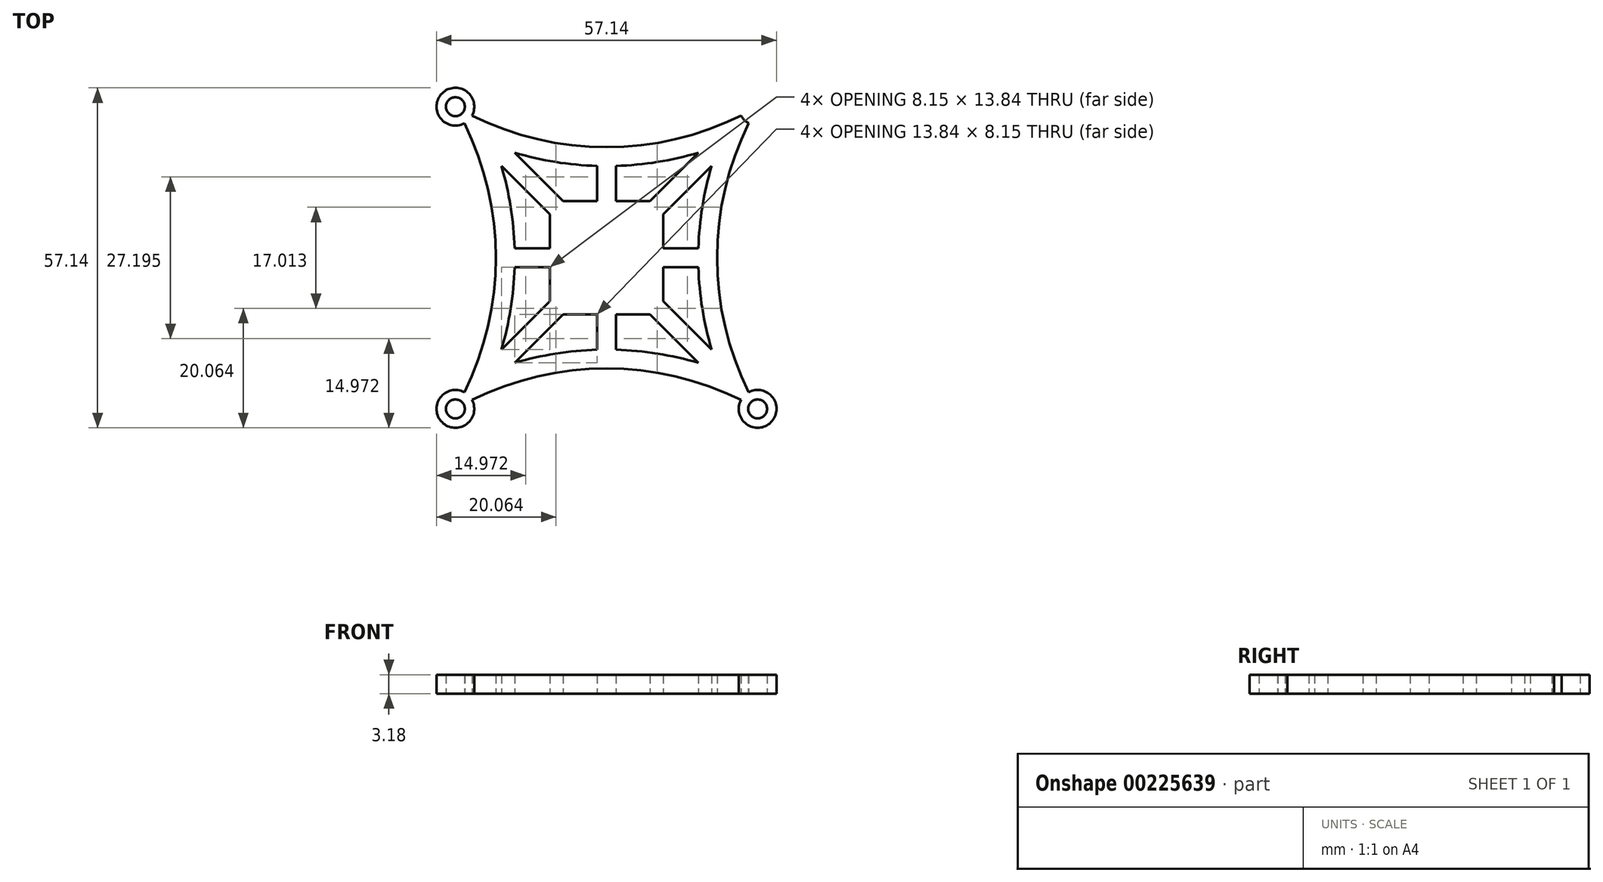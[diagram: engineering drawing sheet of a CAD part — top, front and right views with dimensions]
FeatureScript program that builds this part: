
annotation { "Feature Type Name" : "Feature", "Feature Type Description" : "" }
export const myFeature = defineFeature(function(context is Context, id is Id, definition is map)
    precondition{}
    {
        {
            var Q0;
            Q0=qCreatedBy(makeId("Top.planeOp"),FACE);
            var sketch = newSketch(context, id + "F0", { "sketchPlane" : qUnion([Q0])});
            skPoint(sketch, "E0.middle", {"position": v(0, 0) * mm});
            skArc(sketch, "E1", {"start": v(-25.4, -25.4) * mm, "mid": v(-18.6, 0) * mm, "end": v(-25.4, 25.4) * mm});
            skArc(sketch, "E2", {"start": v(25.4, -25.4) * mm, "mid": v(0, -18.6) * mm, "end": v(-25.4, -25.4) * mm});
            skArc(sketch, "E3.MirrorCS", {"start": v(25.4, 25.4) * mm, "mid": v(0, 18.6) * mm, "end": v(-25.4, 25.4) * mm});
            skArc(sketch, "E4.MirrorCS", {"start": v(25.4, -25.4) * mm, "mid": v(18.6, 0) * mm, "end": v(25.4, 25.4) * mm});
            skCircle(sketch, "E5", {"center": v(-25.4, 25.4) * mm, "radius": 3.18 * mm});
            skCircle(sketch, "E6", {"center": v(-25.4, 25.4) * mm, "radius": 1.59 * mm});
            skCircle(sketch, "E7.MirrorC", {"center": v(25.4, 25.4) * mm, "radius": 3.18 * mm});
            skCircle(sketch, "E8.MirrorC", {"center": v(25.4, 25.4) * mm, "radius": 1.59 * mm});
            skCircle(sketch, "E9.MirrorC", {"center": v(25.4, -25.4) * mm, "radius": 3.18 * mm});
            skCircle(sketch, "E10.MirrorC", {"center": v(25.4, -25.4) * mm, "radius": 1.59 * mm});
            skCircle(sketch, "E11.MirrorC", {"center": v(-25.4, -25.4) * mm, "radius": 3.18 * mm});
            skCircle(sketch, "E12.MirrorC", {"center": v(-25.4, -25.4) * mm, "radius": 1.59 * mm});
            skArc(sketch, "E13.0", {"start": v(18.8, 18.8) * mm, "mid": v(0, 15.42) * mm, "end": v(-18.8, 18.8) * mm});
            skArc(sketch, "E13.1", {"start": v(18.8, -18.8) * mm, "mid": v(15.42, 0) * mm, "end": v(18.8, 18.8) * mm});
            skArc(sketch, "E13.2", {"start": v(18.8, -18.8) * mm, "mid": v(0, -15.42) * mm, "end": v(-18.8, -18.8) * mm});
            skArc(sketch, "E13.3", {"start": v(-18.8, -18.8) * mm, "mid": v(-15.42, 0) * mm, "end": v(-18.8, 18.8) * mm});
            skLineSegment(sketch, "E14.top", {"start": v(-1.59, 15.88) * mm, "end": v(1.59, 15.88) * mm});
            skLineSegment(sketch, "E14.left", {"start": v(-1.59, 12.7) * mm, "end": v(-1.59, 15.88) * mm});
            skLineSegment(sketch, "E14.right", {"start": v(1.59, 12.7) * mm, "end": v(1.59, 15.88) * mm});
            skPoint(sketch, "E14.middle", {"position": v(0, 14.29) * mm});
            skLineSegment(sketch, "E15.MirrorCS", {"start": v(1.59, -12.7) * mm, "end": v(1.59, -15.88) * mm});
            skLineSegment(sketch, "E16.MirrorCS", {"start": v(-1.59, -15.88) * mm, "end": v(1.59, -15.88) * mm});
            skLineSegment(sketch, "E17.MirrorCS", {"start": v(-1.59, -12.7) * mm, "end": v(-1.59, -15.88) * mm});
            skLineSegment(sketch, "E18.bottom", {"start": v(-12.7, 1.59) * mm, "end": v(-15.88, 1.59) * mm});
            skLineSegment(sketch, "E18.top", {"start": v(-12.7, -1.59) * mm, "end": v(-15.88, -1.59) * mm});
            skLineSegment(sketch, "E18.right", {"start": v(-15.88, 1.59) * mm, "end": v(-15.88, -1.59) * mm});
            skPoint(sketch, "E18.middle", {"position": v(-14.29, 0) * mm});
            skLineSegment(sketch, "E19.MirrorCS", {"start": v(12.7, 1.59) * mm, "end": v(15.88, 1.59) * mm});
            skLineSegment(sketch, "E20.MirrorCS", {"start": v(12.7, -1.59) * mm, "end": v(15.88, -1.59) * mm});
            skLineSegment(sketch, "E21.MirrorCS", {"start": v(15.88, 1.59) * mm, "end": v(15.88, -1.59) * mm});
            skPoint(sketch, "E22", {"position": v(10.45, 12.7) * mm});
            skPoint(sketch, "E23", {"position": v(12.7, 10.45) * mm});
            skLineSegment(sketch, "E24", {"start": v(10.45, 12.7) * mm, "end": v(15.43, 17.67) * mm});
            skLineSegment(sketch, "E25", {"start": v(12.7, 10.45) * mm, "end": v(17.67, 15.43) * mm});
            skLineSegment(sketch, "E26", {"start": v(17.67, 15.43) * mm, "end": v(15.43, 17.67) * mm});
            skLineSegment(sketch, "E27.MirrorCS", {"start": v(-17.67, 15.43) * mm, "end": v(-15.43, 17.67) * mm});
            skLineSegment(sketch, "E28.MirrorCS", {"start": v(-10.45, 12.7) * mm, "end": v(-15.43, 17.67) * mm});
            skLineSegment(sketch, "E29.MirrorCS", {"start": v(-12.7, 10.45) * mm, "end": v(-17.67, 15.43) * mm});
            skLineSegment(sketch, "E30.MirrorCS", {"start": v(12.7, -10.45) * mm, "end": v(17.67, -15.43) * mm});
            skLineSegment(sketch, "E31.MirrorCS", {"start": v(10.45, -12.7) * mm, "end": v(15.43, -17.67) * mm});
            skLineSegment(sketch, "E32.MirrorCS", {"start": v(17.67, -15.43) * mm, "end": v(15.43, -17.67) * mm});
            skLineSegment(sketch, "E33.MirrorCS", {"start": v(-10.45, -12.7) * mm, "end": v(-15.43, -17.67) * mm});
            skLineSegment(sketch, "E34.MirrorCS", {"start": v(-12.7, -10.45) * mm, "end": v(-17.67, -15.43) * mm});
            skLineSegment(sketch, "E35.bottom", {"start": v(-9.52, 9.53) * mm, "end": v(9.53, 9.53) * mm});
            skLineSegment(sketch, "E35.top", {"start": v(-9.53, -9.53) * mm, "end": v(9.53, -9.53) * mm});
            skLineSegment(sketch, "E35.left", {"start": v(-9.52, 9.53) * mm, "end": v(-9.53, -9.53) * mm});
            skLineSegment(sketch, "E35.right", {"start": v(9.53, 9.53) * mm, "end": v(9.53, -9.53) * mm});
            skLineSegment(sketch, "E36", {"start": v(-10.45, 12.7) * mm, "end": v(-7.28, 9.53) * mm});
            skLineSegment(sketch, "E37", {"start": v(-7.28, 9.53) * mm, "end": v(-9.53, 7.28) * mm});
            skLineSegment(sketch, "E38", {"start": v(-9.52, 7.28) * mm, "end": v(-12.7, 10.45) * mm});
            skLineSegment(sketch, "E39", {"start": v(1.59, 12.7) * mm, "end": v(1.59, 9.53) * mm});
            skLineSegment(sketch, "E40", {"start": v(1.59, 9.53) * mm, "end": v(-1.59, 9.53) * mm});
            skLineSegment(sketch, "E41", {"start": v(-1.59, 9.53) * mm, "end": v(-1.59, 12.7) * mm});
            skLineSegment(sketch, "E42", {"start": v(12.7, 1.59) * mm, "end": v(9.53, 1.59) * mm});
            skLineSegment(sketch, "E43", {"start": v(9.53, 1.59) * mm, "end": v(9.53, -1.59) * mm});
            skLineSegment(sketch, "E44", {"start": v(9.53, -1.59) * mm, "end": v(12.7, -1.59) * mm});
            skLineSegment(sketch, "E45", {"start": v(12.7, -10.45) * mm, "end": v(9.53, -7.28) * mm});
            skLineSegment(sketch, "E46", {"start": v(9.53, -7.28) * mm, "end": v(7.28, -9.53) * mm});
            skLineSegment(sketch, "E47", {"start": v(7.28, -9.53) * mm, "end": v(10.45, -12.7) * mm});
            skLineSegment(sketch, "E48", {"start": v(1.59, -12.7) * mm, "end": v(1.59, -9.53) * mm});
            skLineSegment(sketch, "E49", {"start": v(1.59, -9.53) * mm, "end": v(-1.59, -9.53) * mm});
            skLineSegment(sketch, "E50", {"start": v(-1.59, -9.53) * mm, "end": v(-1.59, -12.7) * mm});
            skLineSegment(sketch, "E51", {"start": v(-17.67, -15.43) * mm, "end": v(-15.43, -17.67) * mm});
            skLineSegment(sketch, "E52", {"start": v(-10.45, -12.7) * mm, "end": v(-7.28, -9.53) * mm});
            skLineSegment(sketch, "E53", {"start": v(-12.7, -10.45) * mm, "end": v(-9.53, -7.28) * mm});
            skLineSegment(sketch, "E54", {"start": v(-9.53, -7.28) * mm, "end": v(-7.28, -9.53) * mm});
            skLineSegment(sketch, "E55", {"start": v(-12.7, 1.59) * mm, "end": v(-9.53, 1.59) * mm});
            skLineSegment(sketch, "E56", {"start": v(-12.7, -1.59) * mm, "end": v(-9.53, -1.59) * mm});
            skLineSegment(sketch, "E57", {"start": v(10.45, 12.7) * mm, "end": v(7.28, 9.53) * mm});
            skLineSegment(sketch, "E58", {"start": v(7.28, 9.53) * mm, "end": v(9.53, 7.28) * mm});
            skLineSegment(sketch, "E59", {"start": v(9.52, 7.28) * mm, "end": v(12.7, 10.45) * mm});
            skSolve(sketch);
        }
        {
            var Q0;
            {var subQ9=sQuery(id+"F0.wireOp",EDGE,"E37");Q0=makeQuery(id+"F0.imprint","IMPRINT",FACE,{"disambiguationData":[TD([[makeQuery(id+"F0.imprint","IMPRINT",EDGE,{"derivedFrom":subQ9}),1.0]])]});}
            var Q1;
            {var subQ3=sQuery(id+"F0.wireOp",EDGE,"E46");Q1=makeQuery(id+"F0.imprint","IMPRINT",FACE,{"disambiguationData":[TD([[makeQuery(id+"F0.imprint","IMPRINT",EDGE,{"derivedFrom":subQ3}),1.0]])]});}
            var Q2;
            {var subQ3=sQuery(id+"F0.wireOp",EDGE,"E58");Q2=makeQuery(id+"F0.imprint","IMPRINT",FACE,{"disambiguationData":[TD([[makeQuery(id+"F0.imprint","IMPRINT",EDGE,{"derivedFrom":subQ3}),1.0]])]});}
            var Q3;
            {var subQ3=sQuery(id+"F0.wireOp",EDGE,"E37");Q3=makeQuery(id+"F0.imprint","IMPRINT",FACE,{"disambiguationData":[TD([[makeQuery(id+"F0.imprint","IMPRINT",EDGE,{"derivedFrom":subQ3}),-1.0]])]});}
            var Q4;
            {var subQ3=sQuery(id+"F0.wireOp",EDGE,"E54");Q4=makeQuery(id+"F0.imprint","IMPRINT",FACE,{"disambiguationData":[TD([[makeQuery(id+"F0.imprint","IMPRINT",EDGE,{"derivedFrom":subQ3}),-1.0]])]});}
            var Q5;
            Q5=makeQuery(id+"F0.imprint","IMPRINT",FACE,{"disambiguationData":[TD([[makeQuery(id+"F0.imprint","IMPRINT",EDGE,{"derivedFrom":sQuery(id+"F0.wireOp",EDGE,"E33.MirrorCS")}),-1.0]])]});
            var Q6;
            Q6=makeQuery(id+"F0.imprint","IMPRINT",FACE,{"disambiguationData":[TD([[makeQuery(id+"F0.imprint","IMPRINT",EDGE,{"derivedFrom":sQuery(id+"F0.wireOp",EDGE,"E27.MirrorCS")}),-1.0]])]});
            var Q7;
            Q7=makeQuery(id+"F0.imprint","IMPRINT",FACE,{"disambiguationData":[TD([[makeQuery(id+"F0.imprint","IMPRINT",EDGE,{"derivedFrom":sQuery(id+"F0.wireOp",EDGE,"E24")}),-1.0]])]});
            var Q8;
            {var subQ0=sQuery(id+"F0.wireOp",EDGE,"E39");Q8=makeQuery(id+"F0.imprint","IMPRINT",FACE,{"disambiguationData":[TD([[makeQuery(id+"F0.imprint","IMPRINT",EDGE,{"derivedFrom":subQ0}),-1.0]])]});}
            var Q9;
            {var subQ0=sQuery(id+"F0.wireOp",EDGE,"E55");Q9=makeQuery(id+"F0.imprint","IMPRINT",FACE,{"disambiguationData":[TD([[makeQuery(id+"F0.imprint","IMPRINT",EDGE,{"derivedFrom":subQ0}),-1.0]])]});}
            var Q10;
            {var subQ0=sQuery(id+"F0.wireOp",EDGE,"E42");Q10=makeQuery(id+"F0.imprint","IMPRINT",FACE,{"disambiguationData":[TD([[makeQuery(id+"F0.imprint","IMPRINT",EDGE,{"derivedFrom":subQ0}),1.0]])]});}
            var Q11;
            Q11=makeQuery(id+"F0.imprint","IMPRINT",FACE,{"disambiguationData":[TD([[makeQuery(id+"F0.imprint","IMPRINT",EDGE,{"derivedFrom":sQuery(id+"F0.wireOp",EDGE,"E30.MirrorCS")}),-1.0]])]});
            var Q12;
            {var subQ4=sQuery(id+"F0.wireOp",EDGE,"E48");Q12=makeQuery(id+"F0.imprint","IMPRINT",FACE,{"disambiguationData":[TD([[makeQuery(id+"F0.imprint","IMPRINT",EDGE,{"derivedFrom":subQ4}),1.0]])]});}
            var Q13;
            {var subQ5=sQuery(id+"F0.wireOp",EDGE,"E16.MirrorCS");Q13=makeQuery(id+"F0.imprint","IMPRINT",FACE,{"disambiguationData":[TD([[makeQuery(id+"F0.imprint","IMPRINT",EDGE,{"derivedFrom":subQ5}),1.0]])]});}
            var Q14;
            {var subQ5=sQuery(id+"F0.wireOp",EDGE,"E18.right");Q14=makeQuery(id+"F0.imprint","IMPRINT",FACE,{"disambiguationData":[TD([[makeQuery(id+"F0.imprint","IMPRINT",EDGE,{"derivedFrom":subQ5}),1.0]])]});}
            var Q15;
            {var subQ5=sQuery(id+"F0.wireOp",EDGE,"E14.top");Q15=makeQuery(id+"F0.imprint","IMPRINT",FACE,{"disambiguationData":[TD([[makeQuery(id+"F0.imprint","IMPRINT",EDGE,{"derivedFrom":subQ5}),-1.0]])]});}
            var Q16;
            {var subQ5=sQuery(id+"F0.wireOp",EDGE,"E21.MirrorCS");Q16=makeQuery(id+"F0.imprint","IMPRINT",FACE,{"disambiguationData":[TD([[makeQuery(id+"F0.imprint","IMPRINT",EDGE,{"derivedFrom":subQ5}),-1.0]])]});}
            var Q17;
            {var subQ3=sQuery(id+"F0.wireOp",EDGE,"E32.MirrorCS");Q17=makeQuery(id+"F0.imprint","IMPRINT",FACE,{"disambiguationData":[TD([[makeQuery(id+"F0.imprint","IMPRINT",EDGE,{"derivedFrom":subQ3}),1.0]])]});}
            var Q18;
            {var subQ3=sQuery(id+"F0.wireOp",EDGE,"E26");Q18=makeQuery(id+"F0.imprint","IMPRINT",FACE,{"disambiguationData":[TD([[makeQuery(id+"F0.imprint","IMPRINT",EDGE,{"derivedFrom":subQ3}),-1.0]])]});}
            var Q19;
            {var subQ3=sQuery(id+"F0.wireOp",EDGE,"E27.MirrorCS");Q19=makeQuery(id+"F0.imprint","IMPRINT",FACE,{"disambiguationData":[TD([[makeQuery(id+"F0.imprint","IMPRINT",EDGE,{"derivedFrom":subQ3}),1.0]])]});}
            var Q20;
            {var subQ3=sQuery(id+"F0.wireOp",EDGE,"E51");Q20=makeQuery(id+"F0.imprint","IMPRINT",FACE,{"disambiguationData":[TD([[makeQuery(id+"F0.imprint","IMPRINT",EDGE,{"derivedFrom":subQ3}),-1.0]])]});}
            var Q21;
            {var subQ54=sQuery(id+"F0.wireOp",EDGE,"E14.top");Q21=makeQuery(id+"F0.imprint","IMPRINT",FACE,{"disambiguationData":[TD([[makeQuery(id+"F0.imprint","IMPRINT",EDGE,{"derivedFrom":subQ54}),1.0]])]});}
            var Q22;
            {var subQ0=sQuery(id+"F0.wireOp",EDGE,"E5");var subQ1=sQuery(id+"F0.wireOp",EDGE,"E1");var subQ2=makeQuery(id+"F0.imprint","INTERSECT",VERTEX,{"derivedFrom":[subQ1,subQ0]});Q22=makeQuery(id+"F0.imprint","IMPRINT",FACE,{"disambiguationData":[TD([[makeQuery(id+"F0.imprint","IMPRINT",EDGE,{"disambiguationData":[TD([[subQ2,-1.0]])],"derivedFrom":subQ1}),-1.0]])]});}
            var Q23;
            {var subQ0=sQuery(id+"F0.wireOp",EDGE,"E7.MirrorC");var subQ1=sQuery(id+"F0.wireOp",EDGE,"E3.MirrorCS");var subQ2=makeQuery(id+"F0.imprint","INTERSECT",VERTEX,{"derivedFrom":[subQ1,subQ0]});Q23=makeQuery(id+"F0.imprint","IMPRINT",FACE,{"disambiguationData":[TD([[makeQuery(id+"F0.imprint","IMPRINT",EDGE,{"disambiguationData":[TD([[subQ2,1.0]])],"derivedFrom":subQ1}),1.0]])]});}
            var Q24;
            {var subQ0=sQuery(id+"F0.wireOp",EDGE,"E9.MirrorC");var subQ1=sQuery(id+"F0.wireOp",EDGE,"E2");var subQ2=makeQuery(id+"F0.imprint","INTERSECT",VERTEX,{"derivedFrom":[subQ1,subQ0]});Q24=makeQuery(id+"F0.imprint","IMPRINT",FACE,{"disambiguationData":[TD([[makeQuery(id+"F0.imprint","IMPRINT",EDGE,{"disambiguationData":[TD([[subQ2,1.0]])],"derivedFrom":subQ1}),-1.0]])]});}
            var Q25;
            {var subQ0=sQuery(id+"F0.wireOp",EDGE,"E11.MirrorC");var subQ1=sQuery(id+"F0.wireOp",EDGE,"E1");var subQ2=makeQuery(id+"F0.imprint","INTERSECT",VERTEX,{"derivedFrom":[subQ1,subQ0]});Q25=makeQuery(id+"F0.imprint","IMPRINT",FACE,{"disambiguationData":[TD([[makeQuery(id+"F0.imprint","IMPRINT",EDGE,{"disambiguationData":[TD([[subQ2,1.0]])],"derivedFrom":subQ1}),-1.0]])]});}
            var Q26;
            {var subQ0=sQuery(id+"F0.wireOp",EDGE,"E11.MirrorC");var subQ1=sQuery(id+"F0.wireOp",EDGE,"E1");var subQ2=makeQuery(id+"F0.imprint","INTERSECT",VERTEX,{"derivedFrom":[subQ1,subQ0]});Q26=makeQuery(id+"F0.imprint","IMPRINT",FACE,{"disambiguationData":[TD([[makeQuery(id+"F0.imprint","IMPRINT",EDGE,{"disambiguationData":[TD([[subQ2,1.0]])],"derivedFrom":subQ1}),1.0]])]});}
            var Q27;
            {var subQ0=sQuery(id+"F0.wireOp",EDGE,"E5");var subQ1=sQuery(id+"F0.wireOp",EDGE,"E1");var subQ2=makeQuery(id+"F0.imprint","INTERSECT",VERTEX,{"derivedFrom":[subQ1,subQ0]});Q27=makeQuery(id+"F0.imprint","IMPRINT",FACE,{"disambiguationData":[TD([[makeQuery(id+"F0.imprint","IMPRINT",EDGE,{"disambiguationData":[TD([[subQ2,-1.0]])],"derivedFrom":subQ1}),1.0]])]});}
            var Q28;
            {var subQ0=sQuery(id+"F0.wireOp",EDGE,"E7.MirrorC");var subQ1=sQuery(id+"F0.wireOp",EDGE,"E3.MirrorCS");var subQ2=makeQuery(id+"F0.imprint","INTERSECT",VERTEX,{"derivedFrom":[subQ1,subQ0]});Q28=makeQuery(id+"F0.imprint","IMPRINT",FACE,{"disambiguationData":[TD([[makeQuery(id+"F0.imprint","IMPRINT",EDGE,{"disambiguationData":[TD([[subQ2,1.0]])],"derivedFrom":subQ1}),-1.0]])]});}
            var Q29;
            {var subQ0=sQuery(id+"F0.wireOp",EDGE,"E9.MirrorC");var subQ1=sQuery(id+"F0.wireOp",EDGE,"E2");var subQ2=makeQuery(id+"F0.imprint","INTERSECT",VERTEX,{"derivedFrom":[subQ1,subQ0]});Q29=makeQuery(id+"F0.imprint","IMPRINT",FACE,{"disambiguationData":[TD([[makeQuery(id+"F0.imprint","IMPRINT",EDGE,{"disambiguationData":[TD([[subQ2,1.0]])],"derivedFrom":subQ1}),1.0]])]});}
            extrude(context, id + "F1", {"entities" : qUnion([Q0, Q1, Q2, Q3, Q4, Q5, Q6, Q7, Q8, Q9, Q10, Q11, Q12, Q13, Q14, Q15, Q16, Q17, Q18, Q19, Q20, Q21, Q22, Q23, Q24, Q25, Q26, Q27, Q28, Q29]), "depth" : 3.17 * mm});
        }
    });
